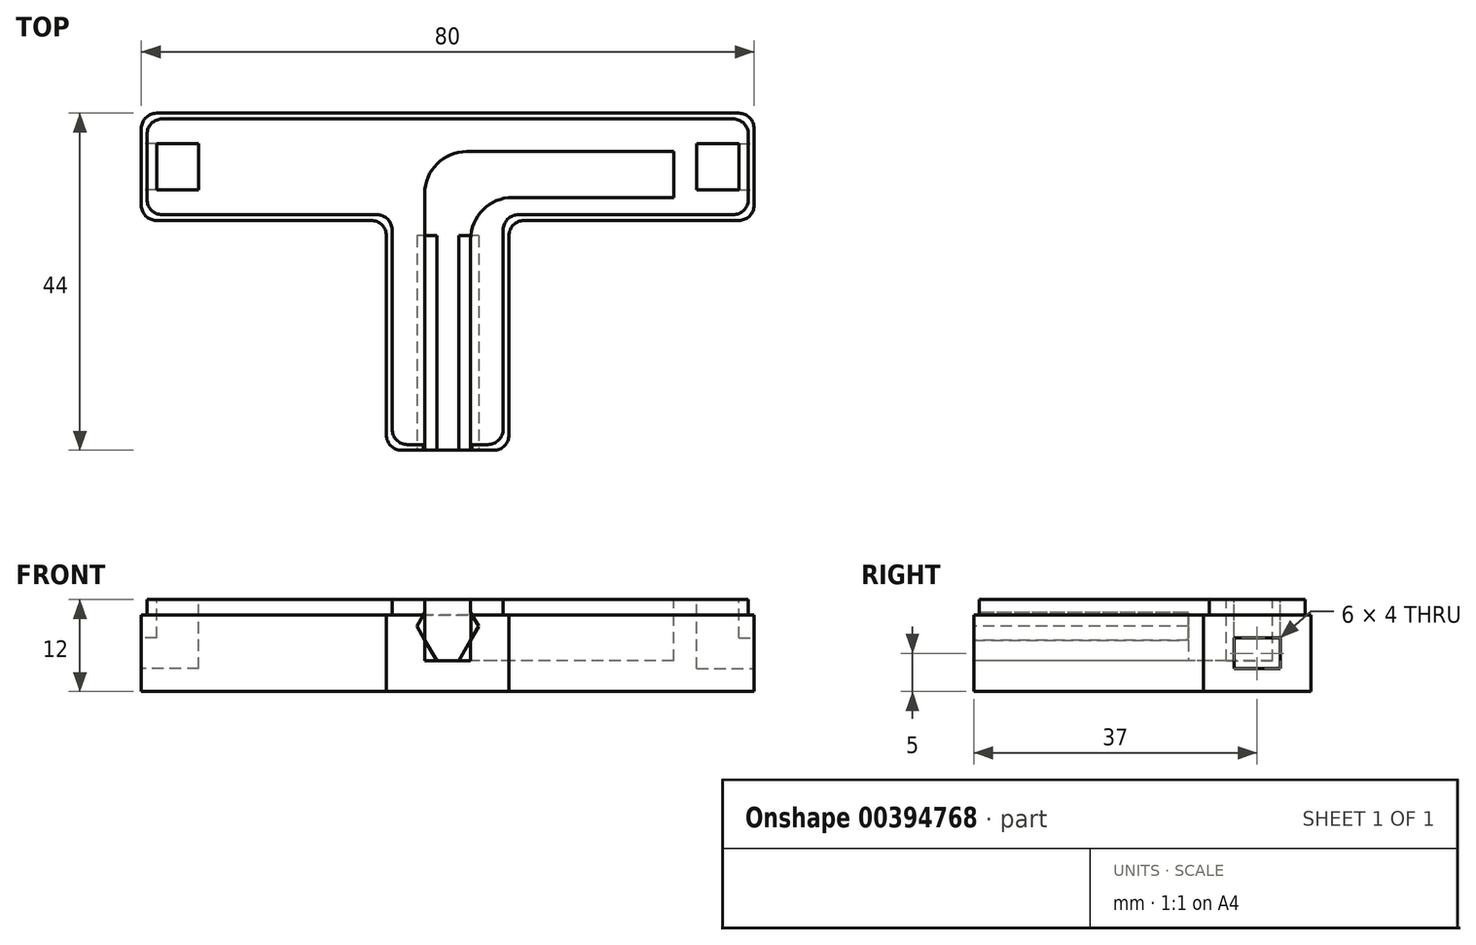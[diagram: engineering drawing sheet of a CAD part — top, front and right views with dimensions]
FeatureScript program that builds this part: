
annotation { "Feature Type Name" : "Feature", "Feature Type Description" : "" }
export const myFeature = defineFeature(function(context is Context, id is Id, definition is map)
    precondition{}
    {
        {
            var Q0;
            Q0=qCreatedBy(makeId("Top.planeOp"),FACE);
            var sketch = newSketch(context, id + "F0", { "sketchPlane" : qUnion([Q0])});
            skLineSegment(sketch, "E0", {"start": v(10, 0) * mm, "end": v(35, 0) * mm});
            skLineSegment(sketch, "E1", {"start": v(-10, 0) * mm, "end": v(-35, 0) * mm});
            skLineSegment(sketch, "E2", {"start": v(-37, 2) * mm, "end": v(-37, 12) * mm});
            skLineSegment(sketch, "E3", {"start": v(37, 2) * mm, "end": v(37, 12) * mm});
            skLineSegment(sketch, "E4", {"start": v(-35, 14) * mm, "end": v(35, 14) * mm});
            skPoint(sketch, "E5.visualSharp", {"position": v(-37, 14) * mm});
            skArc(sketch, "E5.filletArc", {"start": v(-35, 14) * mm, "mid": v(-36.41, 13.41) * mm, "end": v(-37, 12) * mm});
            skPoint(sketch, "E6.visualSharp", {"position": v(37, 14) * mm});
            skArc(sketch, "E6.filletArc", {"start": v(37, 12) * mm, "mid": v(36.41, 13.41) * mm, "end": v(35, 14) * mm});
            skPoint(sketch, "E7.visualSharp", {"position": v(37, 0) * mm});
            skArc(sketch, "E7.filletArc", {"start": v(35, 0) * mm, "mid": v(36.41, 0.59) * mm, "end": v(37, 2) * mm});
            skPoint(sketch, "E8.visualSharp", {"position": v(-37, 0) * mm});
            skArc(sketch, "E8.filletArc", {"start": v(-37, 2) * mm, "mid": v(-36.41, 0.59) * mm, "end": v(-35, 0) * mm});
            skLineSegment(sketch, "E9", {"start": v(-8, -2) * mm, "end": v(-8, -28) * mm});
            skLineSegment(sketch, "E10", {"start": v(8, -2) * mm, "end": v(8, -28) * mm});
            skLineSegment(sketch, "E11", {"start": v(-6, -30) * mm, "end": v(6, -30) * mm});
            skPoint(sketch, "E12.visualSharp", {"position": v(-8, -30) * mm});
            skArc(sketch, "E12.filletArc", {"start": v(-8, -28) * mm, "mid": v(-7.41, -29.41) * mm, "end": v(-6, -30) * mm});
            skPoint(sketch, "E13.visualSharp", {"position": v(8, -30) * mm});
            skArc(sketch, "E13.filletArc", {"start": v(6, -30) * mm, "mid": v(7.41, -29.41) * mm, "end": v(8, -28) * mm});
            skPoint(sketch, "E14.newPointA", {"position": v(0, 0) * mm});
            skPoint(sketch, "E14.newPointB", {"position": v(8, 0) * mm});
            skArc(sketch, "E14.filletArc", {"start": v(10, 0) * mm, "mid": v(8.59, -0.59) * mm, "end": v(8, -2) * mm});
            skPoint(sketch, "E15.newPointB", {"position": v(-8, 0) * mm});
            skArc(sketch, "E15.filletArc", {"start": v(-8, -2) * mm, "mid": v(-8.59, -0.59) * mm, "end": v(-10, 0) * mm});
            skLineSegment(sketch, "E16", {"start": v(0, 0) * mm, "end": v(38, 0) * mm});
            skLineSegment(sketch, "E17", {"start": v(0, 0) * mm, "end": v(-38, 0) * mm});
            skLineSegment(sketch, "E18", {"start": v(-40, 2) * mm, "end": v(-40, 12) * mm});
            skLineSegment(sketch, "E19", {"start": v(-38, 14) * mm, "end": v(38, 14) * mm});
            skLineSegment(sketch, "E20", {"start": v(40, 12) * mm, "end": v(40, 2) * mm});
            skPoint(sketch, "E21.visualSharp", {"position": v(40, 14) * mm});
            skArc(sketch, "E21.filletArc", {"start": v(40, 12) * mm, "mid": v(39.41, 13.41) * mm, "end": v(38, 14) * mm});
            skPoint(sketch, "E22.visualSharp", {"position": v(40, 0) * mm});
            skArc(sketch, "E22.filletArc", {"start": v(38, 0) * mm, "mid": v(39.41, 0.59) * mm, "end": v(40, 2) * mm});
            skPoint(sketch, "E23.visualSharp", {"position": v(-40, 0) * mm});
            skArc(sketch, "E23.filletArc", {"start": v(-40, 2) * mm, "mid": v(-39.41, 0.59) * mm, "end": v(-38, 0) * mm});
            skPoint(sketch, "E24.visualSharp", {"position": v(-40, 14) * mm});
            skArc(sketch, "E24.filletArc", {"start": v(-38, 14) * mm, "mid": v(-39.41, 13.41) * mm, "end": v(-40, 12) * mm});
            skSolve(sketch);
        }
        {
            var Q0;
            Q0=makeQuery(id+"F0.imprint","IMPRINT",FACE,{"disambiguationData":[TD([[makeQuery(id+"F0.imprint","IMPRINT",EDGE,{"derivedFrom":sQuery(id+"F0.wireOp",EDGE,"E0")}),1.0]])]});
            var Q1;
            Q1=makeQuery(id+"F0.imprint","IMPRINT",FACE,{"disambiguationData":[TD([[makeQuery(id+"F0.imprint","IMPRINT",EDGE,{"derivedFrom":sQuery(id+"F0.wireOp",EDGE,"E2")}),1.0]])]});
            var Q2;
            Q2=makeQuery(id+"F0.imprint","IMPRINT",FACE,{"disambiguationData":[TD([[makeQuery(id+"F0.imprint","IMPRINT",EDGE,{"derivedFrom":sQuery(id+"F0.wireOp",EDGE,"E3")}),-1.0]])]});
            var Q3;
            Q3=makeQuery(id+"F0.imprint","IMPRINT",FACE,{"disambiguationData":[TD([[makeQuery(id+"F0.imprint","IMPRINT",EDGE,{"derivedFrom":sQuery(id+"F0.wireOp",EDGE,"E2")}),-1.0]])]});
            var Q4;
            Q4=makeQuery(id+"F0.imprint","IMPRINT",FACE,{"disambiguationData":[TD([[makeQuery(id+"F0.imprint","IMPRINT",EDGE,{"derivedFrom":sQuery(id+"F0.wireOp",EDGE,"E9")}),1.0]])]});
            extrude(context, id + "F1", {"entities" : qUnion([Q0, Q1, Q2, Q3, Q4]), "depth" : 12 * mm});
        }
        {
            var Q0;
            Q0=makeQuery(id+"F1.opExtrude","CAP_FACE",FACE,{"disambiguationData":[OSD([sQuery(id+"F0.wireOp",EDGE,"E0"),sQuery(id+"F0.wireOp",EDGE,"E1"),sQuery(id+"F0.wireOp",EDGE,"E2"),sQuery(id+"F0.wireOp",EDGE,"E3"),sQuery(id+"F0.wireOp",EDGE,"E4"),sQuery(id+"F0.wireOp",EDGE,"E5.filletArc"),sQuery(id+"F0.wireOp",EDGE,"E6.filletArc"),sQuery(id+"F0.wireOp",EDGE,"E7.filletArc"),sQuery(id+"F0.wireOp",EDGE,"E8.filletArc"),sQuery(id+"F0.wireOp",EDGE,"E9"),sQuery(id+"F0.wireOp",EDGE,"E10"),sQuery(id+"F0.wireOp",EDGE,"E11"),sQuery(id+"F0.wireOp",EDGE,"E12.filletArc"),sQuery(id+"F0.wireOp",EDGE,"E13.filletArc"),sQuery(id+"F0.wireOp",EDGE,"E14.filletArc"),sQuery(id+"F0.wireOp",EDGE,"E15.filletArc")])],"isStart":false});
            var sketch = newSketch(context, id + "F2", { "sketchPlane" : qUnion([Q0])});
            skLineSegment(sketch, "E25", {"start": v(37, 12) * mm, "end": v(33, 12) * mm});
            skLineSegment(sketch, "E26", {"start": v(33, 12) * mm, "end": v(33, 9) * mm});
            skLineSegment(sketch, "E27", {"start": v(29.5, 9) * mm, "end": v(2.5, 9) * mm});
            skLineSegment(sketch, "E28", {"start": v(-3, 3.5) * mm, "end": v(-3, -30) * mm});
            skLineSegment(sketch, "E29", {"start": v(29.5, 3) * mm, "end": v(8.5, 3) * mm});
            skLineSegment(sketch, "E30", {"start": v(3, -2.5) * mm, "end": v(3, -30) * mm});
            skPoint(sketch, "E31.start.orphan", {"position": v(-3, 9) * mm});
            skPoint(sketch, "E32.orphan", {"position": v(3, 3) * mm});
            skLineSegment(sketch, "E33", {"start": v(-3, -30) * mm, "end": v(3, -30) * mm});
            skLineSegment(sketch, "E34", {"start": v(8.5, 3) * mm, "end": v(29.5, 3) * mm});
            skLineSegment(sketch, "E35", {"start": v(29.5, 3) * mm, "end": v(29.5, 9) * mm});
            skArc(sketch, "E36", {"start": v(2.5, 9) * mm, "mid": v(-1.39, 7.39) * mm, "end": v(-3, 3.5) * mm});
            skArc(sketch, "E37", {"start": v(8.5, 3) * mm, "mid": v(4.61, 1.39) * mm, "end": v(3, -2.5) * mm});
            skPoint(sketch, "E38.orphan", {"position": v(7.75, 3) * mm});
            skSolve(sketch);
        }
        {
            var Q0;
            Q0 = qSketchRegion(id + "F2", true);
            extrude(context, id + "F3", {"entities" : qUnion([Q0]), "operationType" : NewBodyOperationType.REMOVE, "oppositeDirection" : true, "depth" : 8 * mm});
        }
        {
            var Q0;
            Q0=makeQuery(id+"F1.opExtrude","SWEPT_FACE",FACE,{"disambiguationData":[OSD([sQuery(id+"F0.wireOp",EDGE,"E11")])]});
            var sketch = newSketch(context, id + "F4", { "sketchPlane" : qUnion([Q0])});
            skPoint(sketch, "E39.endSnap0", {"position": v(0, 4) * mm});
            skCircle(sketch, "E40.cCircle", {"center": v(0, 8.5) * mm, "radius": 4.03 * mm, "construction": true});
            skLineSegment(sketch, "E40.0", {"start": v(2.02, 5.02) * mm, "end": v(-2.02, 5.02) * mm});
            skLineSegment(sketch, "E40.1", {"start": v(-2.02, 5.02) * mm, "end": v(-4.03, 8.5) * mm});
            skLineSegment(sketch, "E40.2", {"start": v(-4.03, 8.5) * mm, "end": v(-2.02, 12) * mm});
            skLineSegment(sketch, "E40.3", {"start": v(-2.02, 12) * mm, "end": v(2.02, 12) * mm});
            skLineSegment(sketch, "E40.4", {"start": v(2.02, 12) * mm, "end": v(4.03, 8.5) * mm});
            skLineSegment(sketch, "E40.5", {"start": v(4.03, 8.5) * mm, "end": v(2.02, 5.02) * mm});
            skSolve(sketch);
        }
        {
            var Q0;
            Q0 = qSketchRegion(id + "F4", true);
            extrude(context, id + "F5", {"entities" : qUnion([Q0]), "operationType" : NewBodyOperationType.REMOVE, "oppositeDirection" : true, "depth" : 28 * mm});
        }
        {
            var Q0;
            Q0=makeQuery(id+"F1.opExtrude","SWEPT_FACE",FACE,{"disambiguationData":[OSD([sQuery(id+"F0.wireOp",EDGE,"E11")])]});
            var sketch = newSketch(context, id + "F6", { "sketchPlane" : qUnion([Q0])});
            skLineSegment(sketch, "E41", {"start": v(-4.03, 8.5) * mm, "end": v(-1.43, 4) * mm});
            skLineSegment(sketch, "E42", {"start": v(-1.43, 4) * mm, "end": v(-3, 4) * mm});
            skLineSegment(sketch, "E43", {"start": v(-3, 4) * mm, "end": v(-3, 6.72) * mm});
            skLineSegment(sketch, "E44", {"start": v(4.03, 8.5) * mm, "end": v(3, 6.72) * mm});
            skLineSegment(sketch, "E45", {"start": v(4.03, 8.5) * mm, "end": v(1.43, 4) * mm});
            skLineSegment(sketch, "E46", {"start": v(1.43, 4) * mm, "end": v(3, 4) * mm});
            skLineSegment(sketch, "E47", {"start": v(3, 4) * mm, "end": v(3, 6.72) * mm});
            skSolve(sketch);
        }
        {
            var Q0;
            Q0 = qSketchRegion(id + "F6", true);
            extrude(context, id + "F7", {"entities" : qUnion([Q0]), "oppositeDirection" : true, "depth" : 28 * mm});
        }
        {
            var Q0;
            Q0=makeQuery(id+"F2.imprint","IMPRINT",FACE,{"disambiguationData":[TD([[makeQuery(id+"F2.imprint","IMPRINT",EDGE,{"derivedFrom":sQuery(id+"F2.wireOp",EDGE,"E27")}),-1.0]])]});
            var sketch = newSketch(context, id + "F8", { "sketchPlane" : qUnion([Q0])});
            skLineSegment(sketch, "E48", {"start": v(0, 0) * mm, "end": v(35, 0) * mm});
            skLineSegment(sketch, "E49", {"start": v(35, 0) * mm, "end": v(35, 4) * mm});
            skLineSegment(sketch, "E50", {"start": v(35, 14) * mm, "end": v(35, 10) * mm});
            skLineSegment(sketch, "E51", {"start": v(35, 10) * mm, "end": v(38, 10) * mm});
            skLineSegment(sketch, "E52", {"start": v(38, 10) * mm, "end": v(38, 4) * mm});
            skLineSegment(sketch, "E53", {"start": v(0, 0) * mm, "end": v(-35, 0) * mm});
            skLineSegment(sketch, "E54", {"start": v(-35, 0) * mm, "end": v(-35, 4) * mm});
            skLineSegment(sketch, "E55", {"start": v(-35, 10) * mm, "end": v(-38, 10) * mm});
            skLineSegment(sketch, "E56", {"start": v(-38, 10) * mm, "end": v(-38, 4) * mm});
            skLineSegment(sketch, "E57", {"start": v(-38, 4) * mm, "end": v(-35, 4) * mm});
            skLineSegment(sketch, "E58", {"start": v(-38, 10) * mm, "end": v(-33, 10) * mm});
            skLineSegment(sketch, "E59", {"start": v(-38, 4) * mm, "end": v(-33, 4) * mm});
            skPoint(sketch, "E59.endSnap0", {"position": v(-36.5, 4) * mm});
            skLineSegment(sketch, "E60", {"start": v(38, 10) * mm, "end": v(33, 10) * mm});
            skPoint(sketch, "E60.endSnap0", {"position": v(36.5, 10) * mm});
            skLineSegment(sketch, "E61", {"start": v(38, 10) * mm, "end": v(32.5, 10) * mm});
            skPoint(sketch, "E61.endSnap0", {"position": v(35.5, 10) * mm});
            skLineSegment(sketch, "E62", {"start": v(32.5, 10) * mm, "end": v(32.5, 4.63) * mm});
            skLineSegment(sketch, "E63", {"start": v(32.5, 4) * mm, "end": v(32.4, 4) * mm});
            skLineSegment(sketch, "E64", {"start": v(32.5, 4.63) * mm, "end": v(32.5, 4) * mm});
            skPoint(sketch, "E64.endSnap0", {"position": v(32.4, 4) * mm});
            skPoint(sketch, "E65.orphan", {"position": v(31.81, 4) * mm});
            skPoint(sketch, "E66.orphan", {"position": v(33, 4) * mm});
            skLineSegment(sketch, "E67", {"start": v(38, 4) * mm, "end": v(32.5, 4) * mm});
            skLineSegment(sketch, "E68", {"start": v(-38, 10) * mm, "end": v(-32.5, 10) * mm});
            skLineSegment(sketch, "E69", {"start": v(-32.5, 10) * mm, "end": v(-32.5, 4) * mm});
            skLineSegment(sketch, "E70", {"start": v(-33, 4) * mm, "end": v(-32.5, 4) * mm});
            skSolve(sketch);
        }
        {
            var Q0;
            Q0 = qSketchRegion(id + "F8", true);
            extrude(context, id + "F9", {"entities" : qUnion([Q0]), "operationType" : NewBodyOperationType.REMOVE, "oppositeDirection" : true, "depth" : 8 * mm});
        }
        {
            var Q0;
            Q0=makeQuery(id+"F1.opExtrude","SWEPT_FACE",FACE,{"disambiguationData":[OSD([sQuery(id+"F0.wireOp",EDGE,"E20")])]});
            var sketch = newSketch(context, id + "F10", { "sketchPlane" : qUnion([Q0])});
            skLineSegment(sketch, "E71", {"start": v(2, 12) * mm, "end": v(4, 12) * mm});
            skLineSegment(sketch, "E72", {"start": v(4, 12) * mm, "end": v(4, 4) * mm});
            skLineSegment(sketch, "E73", {"start": v(10, 4) * mm, "end": v(10, 7) * mm});
            skLineSegment(sketch, "E74", {"start": v(10, 7) * mm, "end": v(4, 7) * mm});
            skLineSegment(sketch, "E75", {"start": v(10, 7) * mm, "end": v(10, 3) * mm});
            skLineSegment(sketch, "E76", {"start": v(10, 3) * mm, "end": v(4, 3) * mm});
            skLineSegment(sketch, "E77", {"start": v(4, 4) * mm, "end": v(4, 3) * mm});
            skLineSegment(sketch, "E78", {"start": v(10, 3) * mm, "end": v(10, 5) * mm});
            skSolve(sketch);
        }
        {
            var Q0;
            {var subQ2=sQuery(id+"F10.wireOp",EDGE,"E74");Q0=makeQuery(id+"F10.imprint","IMPRINT",FACE,{"disambiguationData":[TD([[makeQuery(id+"F10.imprint","IMPRINT",EDGE,{"derivedFrom":subQ2}),1.0]])]});}
            var Q1;
            Q1=makeQuery(id+"F9.boolean.opBoolean","COPY",FACE,{"derivedFrom":makeQuery(id+"F9.opExtrude","SWEPT_FACE",FACE,{"disambiguationData":[OSD([sQuery(id+"F8.wireOp",EDGE,"E62"),sQuery(id+"F8.wireOp",EDGE,"E64")])]})});
            extrude(context, id + "F11", {"entities" : qUnion([Q0]), "operationType" : NewBodyOperationType.REMOVE, "endBound" : BoundingType.UP_TO_SURFACE, "oppositeDirection" : true, "endBoundEntityFace" : qUnion([Q1]), "depth" : 7 * mm});
        }
        {
            var Q0;
            Q0=makeQuery(id+"F1.opExtrude","SWEPT_FACE",FACE,{"disambiguationData":[OSD([sQuery(id+"F0.wireOp",EDGE,"E18")])]});
            var sketch = newSketch(context, id + "F12", { "sketchPlane" : qUnion([Q0])});
            skLineSegment(sketch, "E79", {"start": v(-2, 12) * mm, "end": v(-4, 12) * mm});
            skLineSegment(sketch, "E80", {"start": v(-4, 12) * mm, "end": v(-4, 9) * mm});
            skLineSegment(sketch, "E81", {"start": v(-4, 3) * mm, "end": v(-10, 3) * mm});
            skLineSegment(sketch, "E82", {"start": v(-4, 3) * mm, "end": v(-4, 7) * mm});
            skLineSegment(sketch, "E83", {"start": v(-4, 7) * mm, "end": v(-10, 7) * mm});
            skLineSegment(sketch, "E84", {"start": v(-10, 3) * mm, "end": v(-10, 7) * mm});
            skSolve(sketch);
        }
        {
            var Q0;
            Q0 = qSketchRegion(id + "F12", true);
            var Q1;
            Q1=makeQuery(id+"F9.boolean.opBoolean","COPY",FACE,{"derivedFrom":makeQuery(id+"F9.opExtrude","SWEPT_FACE",FACE,{"disambiguationData":[OSD([sQuery(id+"F8.wireOp",EDGE,"E69")])]})});
            extrude(context, id + "F13", {"entities" : qUnion([Q0]), "operationType" : NewBodyOperationType.REMOVE, "endBound" : BoundingType.UP_TO_SURFACE, "oppositeDirection" : true, "endBoundEntityFace" : qUnion([Q1]), "depth" : 5 * mm});
        }
        {
            var Q0;
            Q0=makeQuery(id+"F2.imprint","IMPRINT",FACE,{"disambiguationData":[TD([[makeQuery(id+"F2.imprint","IMPRINT",EDGE,{"derivedFrom":sQuery(id+"F2.wireOp",EDGE,"E27")}),-1.0]])]});
            var sketch = newSketch(context, id + "F14", { "sketchPlane" : qUnion([Q0])});
            skLineSegment(sketch, "E85", {"start": v(0, 0) * mm, "end": v(38, 0) * mm});
            skPoint(sketch, "E86.visualSharp", {"position": v(38.5, 0) * mm});
            skLineSegment(sketch, "E87", {"start": v(0, 0) * mm, "end": v(7.25, 0) * mm});
            skLineSegment(sketch, "E88", {"start": v(7.25, -6.4) * mm, "end": v(8, -6.4) * mm});
            skLineSegment(sketch, "E89", {"start": v(37.25, 0.75) * mm, "end": v(9.25, 0.75) * mm});
            skPoint(sketch, "E90.orphan", {"position": v(6.5, 2.94) * mm});
            skLineSegment(sketch, "E91", {"start": v(7.25, -1.25) * mm, "end": v(7.25, -27.25) * mm});
            skPoint(sketch, "E92.end.orphan", {"position": v(6.5, 0) * mm});
            skPoint(sketch, "E93.end.orphan", {"position": v(38.5, 12) * mm});
            skLineSegment(sketch, "E94", {"start": v(39.25, 2.75) * mm, "end": v(39.25, 11.25) * mm});
            skLineSegment(sketch, "E95", {"start": v(37.25, 13.25) * mm, "end": v(-37.25, 13.25) * mm});
            skLineSegment(sketch, "E96", {"start": v(-39.25, 12.5) * mm, "end": v(-39.25, 13.25) * mm});
            skPoint(sketch, "E97.visualSharp", {"position": v(39.25, 0.75) * mm});
            skArc(sketch, "E97.filletArc", {"start": v(37.25, 0.75) * mm, "mid": v(38.66, 1.34) * mm, "end": v(39.25, 2.75) * mm});
            skPoint(sketch, "E98.visualSharp", {"position": v(39.25, 13.25) * mm});
            skArc(sketch, "E98.filletArc", {"start": v(39.25, 11.25) * mm, "mid": v(38.66, 12.66) * mm, "end": v(37.25, 13.25) * mm});
            skPoint(sketch, "E99.visualSharp", {"position": v(-39.25, 13.25) * mm});
            skArc(sketch, "E99.filletArc", {"start": v(-37.25, 13.25) * mm, "mid": v(-38.66, 12.66) * mm, "end": v(-39.25, 11.25) * mm});
            skPoint(sketch, "E100.visualSharp", {"position": v(7.25, 0.75) * mm});
            skArc(sketch, "E100.filletArc", {"start": v(9.25, 0.75) * mm, "mid": v(7.84, 0.16) * mm, "end": v(7.25, -1.25) * mm});
            skLineSegment(sketch, "E101", {"start": v(0, 0) * mm, "end": v(0, -30) * mm});
            skLineSegment(sketch, "E102", {"start": v(0, -30) * mm, "end": v(4.18, -30) * mm});
            skArc(sketch, "E103.filletArc", {"start": v(5.25, -29.25) * mm, "mid": v(6.66, -28.66) * mm, "end": v(7.25, -27.25) * mm});
            skLineSegment(sketch, "E104", {"start": v(0, -30) * mm, "end": v(6, -30) * mm});
            skLineSegment(sketch, "E105", {"start": v(38, 0) * mm, "end": v(10, 0) * mm});
            skPoint(sketch, "E105.endSnap0", {"position": v(3.63, 0) * mm});
            skLineSegment(sketch, "E106", {"start": v(8, -28) * mm, "end": v(8, -2) * mm});
            skPoint(sketch, "E107.orphan", {"position": v(-2.8, 0) * mm});
            skArc(sketch, "E108.filletArc", {"start": v(10, 0) * mm, "mid": v(8.59, -0.59) * mm, "end": v(8, -2) * mm});
            skLineSegment(sketch, "E109", {"start": v(38, 0) * mm, "end": v(40, 0) * mm});
            skLineSegment(sketch, "E110", {"start": v(40, 2) * mm, "end": v(40, 12) * mm});
            skArc(sketch, "E111.filletArc", {"start": v(40, 12) * mm, "mid": v(39.41, 13.41) * mm, "end": v(38, 14) * mm});
            skPoint(sketch, "E112.visualSharp", {"position": v(40, 0) * mm});
            skArc(sketch, "E112.filletArc", {"start": v(38, 0) * mm, "mid": v(39.41, 0.59) * mm, "end": v(40, 2) * mm});
            skPoint(sketch, "E113.visualSharp", {"position": v(8, -30) * mm});
            skArc(sketch, "E113.filletArc", {"start": v(6, -30) * mm, "mid": v(7.41, -29.41) * mm, "end": v(8, -28) * mm});
            skLineSegment(sketch, "E114", {"start": v(0, -30) * mm, "end": v(0, -29.25) * mm});
            skLineSegment(sketch, "E115", {"start": v(0, -29.25) * mm, "end": v(5.25, -29.25) * mm});
            skLineSegment(sketch, "E116", {"start": v(38, 14) * mm, "end": v(-38, 14) * mm});
            skArc(sketch, "E117.filletArc", {"start": v(-38, 14) * mm, "mid": v(-39.41, 13.41) * mm, "end": v(-40, 12) * mm});
            skLineSegment(sketch, "E118", {"start": v(-40, 12) * mm, "end": v(-40, 2) * mm});
            skLineSegment(sketch, "E119", {"start": v(-32.74, 0) * mm, "end": v(-38, 0) * mm});
            skArc(sketch, "E120.filletArc", {"start": v(-40, 2) * mm, "mid": v(-39.41, 0.59) * mm, "end": v(-38, 0) * mm});
            skLineSegment(sketch, "E121", {"start": v(-39.25, 11.25) * mm, "end": v(-39.25, 2.75) * mm});
            skLineSegment(sketch, "E122", {"start": v(-32.74, 0.75) * mm, "end": v(-37.25, 0.75) * mm});
            skArc(sketch, "E123.filletArc", {"start": v(-39.25, 2.75) * mm, "mid": v(-38.66, 1.34) * mm, "end": v(-37.25, 0.75) * mm});
            skLineSegment(sketch, "E124", {"start": v(0, -30) * mm, "end": v(-6, -30) * mm});
            skLineSegment(sketch, "E125", {"start": v(-8, -28) * mm, "end": v(-8, -2) * mm});
            skLineSegment(sketch, "E126", {"start": v(-32.74, 0.75) * mm, "end": v(-9.25, 0.75) * mm});
            skLineSegment(sketch, "E127", {"start": v(-32.74, 0) * mm, "end": v(-10, 0) * mm});
            skLineSegment(sketch, "E128", {"start": v(-8, -30) * mm, "end": v(-7.25, -30) * mm});
            skLineSegment(sketch, "E129", {"start": v(-7.25, -27.25) * mm, "end": v(-7.25, -1.25) * mm});
            skArc(sketch, "E130.filletArc", {"start": v(-8, -2) * mm, "mid": v(-8.59, -0.59) * mm, "end": v(-10, 0) * mm});
            skArc(sketch, "E131.filletArc", {"start": v(-7.25, -1.25) * mm, "mid": v(-7.84, 0.16) * mm, "end": v(-9.25, 0.75) * mm});
            skLineSegment(sketch, "E132", {"start": v(0, -29.25) * mm, "end": v(-5.25, -29.25) * mm});
            skArc(sketch, "E133.filletArc", {"start": v(-7.25, -27.25) * mm, "mid": v(-6.66, -28.66) * mm, "end": v(-5.25, -29.25) * mm});
            skPoint(sketch, "E134.visualSharp", {"position": v(-8, -30) * mm});
            skArc(sketch, "E134.filletArc", {"start": v(-8, -28) * mm, "mid": v(-7.41, -29.41) * mm, "end": v(-6, -30) * mm});
            skSolve(sketch);
        }
        {
            var Q0;
            Q0 = qSketchRegion(id + "F14", true);
            extrude(context, id + "F15", {"entities" : qUnion([Q0]), "operationType" : NewBodyOperationType.REMOVE, "oppositeDirection" : true, "depth" : 2 * mm});
        }
    });
